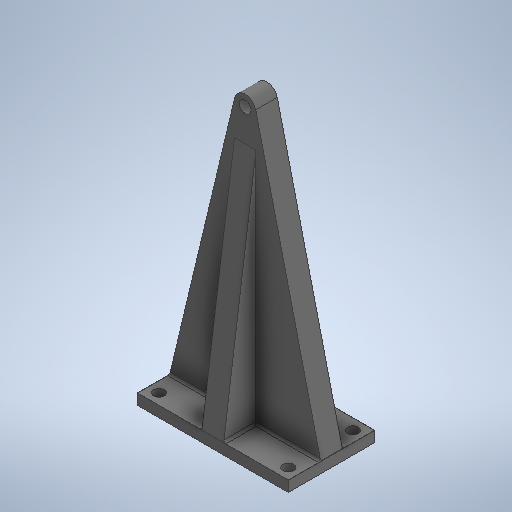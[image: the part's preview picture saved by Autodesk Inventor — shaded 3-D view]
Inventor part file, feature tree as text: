
AUTODESK INVENTOR PART (.ipt)
format: ipt  version: 2025.2 (Build 292293000, 293)  size: 357,376 bytes
history: native  units: mm
features: sketch x9, extrude x6, other x1, mirror x1, fillet x1, hole x1
ambient origin geometry x8: Origin, YZ Plane, XZ Plane, XY Plane, X Axis, Y Axis, Z Axis, Center Point
bodies: Body1 (feature_tree)
feature tree (19):
  other  "Bryła1"
  extrude  "Wyciągnięcie proste1"  Depth=70.0mm
  extrude  "Wyciągnięcie proste6"  Depth=40.0mm
  extrude  "Wyciągnięcie proste7"  Depth=5.0mm TaperAngle=0.0deg
  sketch  "Szkic10"
  extrude  "Wyciągnięcie proste8"  Depth=70.0mm
  sketch  "Szkic12"
  extrude  "Wyciągnięcie proste9"  Depth=10.0mm
  extrude  "Wyciągnięcie proste10"  Depth=130.0mm TaperAngle=0.0deg
  mirror  "Odbij1"
  fillet  "Zaokrąglenie1"  Radius=5.5mm
  hole  "Otwór1"  [1 undecoded]
  sketch  "Szkic1"
  sketch  "Szkic8"
  sketch  "Szkic9"
  sketch  "Szkic11"
  sketch  "Szkic13"
  sketch  "Szkic14"
  sketch  "Szkic16"
note: 1 required parameter value undecoded (feature->parameter linkage not recoverable at this tier; creation-order binding heuristic only, values carry confidence <= 0.55)
